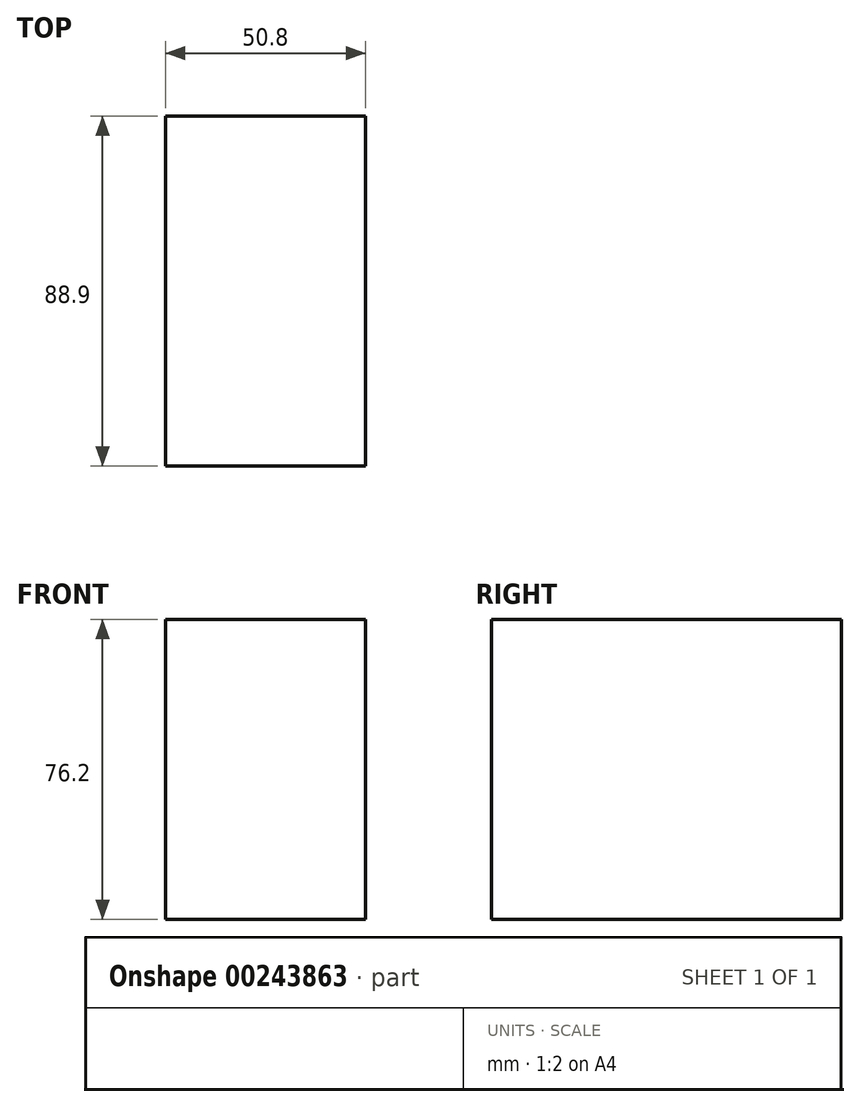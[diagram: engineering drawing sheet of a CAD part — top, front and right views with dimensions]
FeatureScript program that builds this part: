
annotation { "Feature Type Name" : "Feature", "Feature Type Description" : "" }
export const myFeature = defineFeature(function(context is Context, id is Id, definition is map)
    precondition{}
    {
        {
            var Q0;
            Q0=qCreatedBy(makeId("Front.planeOp"),FACE);
            var sketch = newSketch(context, id + "F0", { "sketchPlane" : qUnion([Q0])});
            skLineSegment(sketch, "E0.bottom", {"start": v(-39.25, 37.86) * mm, "end": v(11.55, 37.86) * mm});
            skLineSegment(sketch, "E0.top", {"start": v(-39.25, -38.34) * mm, "end": v(11.55, -38.34) * mm});
            skLineSegment(sketch, "E0.left", {"start": v(-39.25, 37.86) * mm, "end": v(-39.25, -38.34) * mm});
            skLineSegment(sketch, "E0.right", {"start": v(11.55, 37.86) * mm, "end": v(11.55, -38.34) * mm});
            skSolve(sketch);
        }
        {
            var Q0;
            Q0 = qSketchRegion(id + "F0", true);
            extrude(context, id + "F1", {"entities" : qUnion([Q0]), "depth" : 88.9 * mm});
        }
    });
